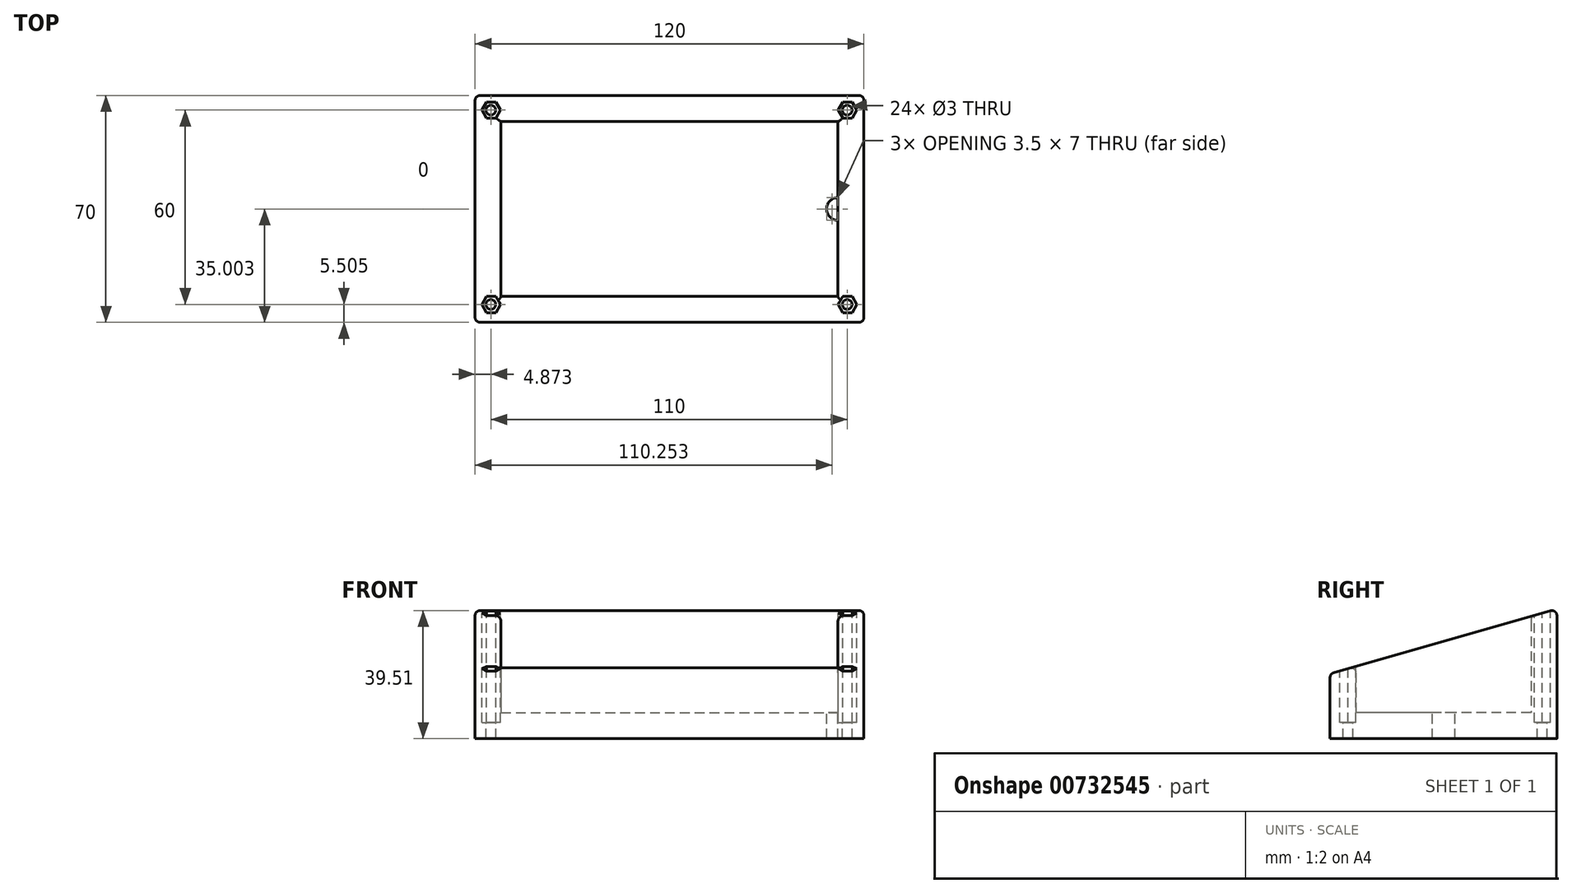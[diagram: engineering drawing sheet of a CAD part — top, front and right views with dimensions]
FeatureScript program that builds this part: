
annotation { "Feature Type Name" : "Feature", "Feature Type Description" : "" }
export const myFeature = defineFeature(function(context is Context, id is Id, definition is map)
    precondition{}
    {
        {
            var Q0;
            Q0=qCreatedBy(makeId("Top.planeOp"),FACE);
            var sketch = newSketch(context, id + "F0", { "sketchPlane" : qUnion([Q0])});
            skLineSegment(sketch, "E0.bottom", {"start": v(-49.4, 44.01) * mm, "end": v(70.6, 44.01) * mm});
            skLineSegment(sketch, "E0.top", {"start": v(-49.4, -25.99) * mm, "end": v(70.6, -25.99) * mm});
            skLineSegment(sketch, "E0.left", {"start": v(-49.4, 44.01) * mm, "end": v(-49.4, -25.99) * mm});
            skLineSegment(sketch, "E0.right", {"start": v(70.6, 44.01) * mm, "end": v(70.6, -25.99) * mm});
            skSolve(sketch);
        }
        {
            var Q0;
            Q0 = qSketchRegion(id + "F0", true);
            extrude(context, id + "F1", {"entities" : qUnion([Q0]), "depth" : 40 * mm, "offsetDistance" : 25 * mm});
        }
        {
            var Q0;
            Q0=makeQuery(id+"F1.opExtrude","SWEPT_FACE",FACE,{"disambiguationData":[OSD([sQuery(id+"F0.wireOp",EDGE,"E0.left")])]});
            var sketch = newSketch(context, id + "F2", { "sketchPlane" : qUnion([Q0])});
            skLineSegment(sketch, "E1", {"start": v(-44.01, 40) * mm, "end": v(25.99, 20) * mm});
            skLineSegment(sketch, "E2", {"start": v(25.99, 20) * mm, "end": v(25.99, 40) * mm});
            skLineSegment(sketch, "E3", {"start": v(25.99, 40) * mm, "end": v(-44.01, 40) * mm});
            skSolve(sketch);
        }
        {
            var Q0;
            Q0 = qSketchRegion(id + "F2", true);
            extrude(context, id + "F3", {"entities" : qUnion([Q0]), "operationType" : NewBodyOperationType.REMOVE, "endBound" : BoundingType.THROUGH_ALL, "oppositeDirection" : true, "depth" : 25 * mm, "offsetDistance" : 25 * mm});
        }
        {
            var Q0;
            Q0=makeQuery(id+"F3.boolean.opBoolean","COPY",FACE,{"derivedFrom":makeQuery(id+"F3.opExtrude","SWEPT_FACE",FACE,{"disambiguationData":[OSD([sQuery(id+"F2.wireOp",EDGE,"E1")])]})});
            shell(context, id + "F4", {"entities" : qUnion([Q0]), "thickness" : 8 * mm});
        }
        {
            var Q0;
            Q0=makeQuery(id+"F1.opExtrude","SWEPT_EDGE",EDGE,{"disambiguationData":[OSD([sQuery(id+"F0.wireOp",EDGE,"E0.top"),sQuery(id+"F0.wireOp",EDGE,"E0.left")])]});
            var Q1;
            Q1=makeQuery(id+"F1.opExtrude","SWEPT_EDGE",EDGE,{"disambiguationData":[OSD([sQuery(id+"F0.wireOp",EDGE,"E0.bottom"),sQuery(id+"F0.wireOp",EDGE,"E0.left")])]});
            var Q2;
            Q2=makeQuery(id+"F1.opExtrude","SWEPT_EDGE",EDGE,{"disambiguationData":[OSD([sQuery(id+"F0.wireOp",EDGE,"E0.bottom"),sQuery(id+"F0.wireOp",EDGE,"E0.right")])]});
            var Q3;
            Q3=makeQuery(id+"F1.opExtrude","SWEPT_EDGE",EDGE,{"disambiguationData":[OSD([sQuery(id+"F0.wireOp",EDGE,"E0.top"),sQuery(id+"F0.wireOp",EDGE,"E0.right")])]});
            var Q4;
            Q4=makeQuery(id+"F3.boolean.opBoolean","COPY",FACE,{"derivedFrom":makeQuery(id+"F3.opExtrude","SWEPT_FACE",FACE,{"disambiguationData":[OSD([sQuery(id+"F2.wireOp",EDGE,"E1")])]})});
            fillet(context, id + "F5", {"entities" : qUnion([Q0, Q1, Q2, Q3, Q4]), "radius" : 1.5 * mm, "tangentPropagation" : true, "allowEdgeOverflow" : false});
        }
        {
            var Q0;
            Q0=qCreatedBy(makeId("Top.planeOp"),FACE);
            cPlane(context, id + "F6", {"entities" : qUnion([Q0]), "cplaneType" : CPlaneType.OFFSET, "offset" : 40 * mm, "width" : 150 * mm, "height" : 150 * mm});
        }
        {
            var Q0;
            Q0=qCreatedBy(id+"F6.planeOp",FACE);
            var sketch = newSketch(context, id + "F7", { "sketchPlane" : qUnion([Q0])});
            skCircle(sketch, "E4.cCircle", {"center": v(-44.47, 39.51) * mm, "radius": 2.5 * mm, "construction": true});
            skLineSegment(sketch, "E4.0", {"start": v(-41.58, 39.51) * mm, "end": v(-43.03, 37.01) * mm});
            skLineSegment(sketch, "E4.1", {"start": v(-43.03, 37.01) * mm, "end": v(-45.91, 37.01) * mm});
            skLineSegment(sketch, "E4.2", {"start": v(-45.91, 37.01) * mm, "end": v(-47.36, 39.51) * mm});
            skLineSegment(sketch, "E4.3", {"start": v(-47.36, 39.51) * mm, "end": v(-45.91, 42.01) * mm});
            skLineSegment(sketch, "E4.4", {"start": v(-45.91, 42.01) * mm, "end": v(-43.03, 42.01) * mm});
            skLineSegment(sketch, "E4.5", {"start": v(-43.03, 42.01) * mm, "end": v(-41.58, 39.51) * mm});
            skPoint(sketch, "E4.0.midPoint", {"position": v(-42.3, 38.26) * mm});
            skCircle(sketch, "E5.cCircle", {"center": v(65.53, 39.51) * mm, "radius": 2.5 * mm, "construction": true});
            skLineSegment(sketch, "E5.0", {"start": v(68.42, 39.51) * mm, "end": v(66.97, 37.01) * mm});
            skLineSegment(sketch, "E5.1", {"start": v(66.97, 37.01) * mm, "end": v(64.09, 37.01) * mm});
            skLineSegment(sketch, "E5.2", {"start": v(64.09, 37.01) * mm, "end": v(62.64, 39.51) * mm});
            skLineSegment(sketch, "E5.3", {"start": v(62.64, 39.51) * mm, "end": v(64.09, 42.01) * mm});
            skLineSegment(sketch, "E5.4", {"start": v(64.09, 42.01) * mm, "end": v(66.97, 42.01) * mm});
            skLineSegment(sketch, "E5.5", {"start": v(66.97, 42.01) * mm, "end": v(68.42, 39.51) * mm});
            skPoint(sketch, "E5.0.midPoint", {"position": v(67.7, 38.26) * mm});
            skCircle(sketch, "E6.cCircle", {"center": v(-44.47, -20.49) * mm, "radius": 2.5 * mm, "construction": true});
            skLineSegment(sketch, "E6.0", {"start": v(-41.58, -20.49) * mm, "end": v(-43.03, -22.99) * mm});
            skLineSegment(sketch, "E6.1", {"start": v(-43.03, -22.99) * mm, "end": v(-45.91, -22.99) * mm});
            skLineSegment(sketch, "E6.2", {"start": v(-45.91, -22.99) * mm, "end": v(-47.36, -20.49) * mm});
            skLineSegment(sketch, "E6.3", {"start": v(-47.36, -20.49) * mm, "end": v(-45.91, -17.99) * mm});
            skLineSegment(sketch, "E6.4", {"start": v(-45.91, -17.99) * mm, "end": v(-43.03, -17.99) * mm});
            skLineSegment(sketch, "E6.5", {"start": v(-43.03, -17.99) * mm, "end": v(-41.58, -20.49) * mm});
            skPoint(sketch, "E6.0.midPoint", {"position": v(-42.3, -21.74) * mm});
            skCircle(sketch, "E7.cCircle", {"center": v(65.53, -20.49) * mm, "radius": 2.5 * mm, "construction": true});
            skLineSegment(sketch, "E7.0", {"start": v(68.42, -20.49) * mm, "end": v(66.97, -22.99) * mm});
            skLineSegment(sketch, "E7.1", {"start": v(66.97, -22.99) * mm, "end": v(64.09, -22.99) * mm});
            skLineSegment(sketch, "E7.2", {"start": v(64.09, -22.99) * mm, "end": v(62.64, -20.49) * mm});
            skLineSegment(sketch, "E7.3", {"start": v(62.64, -20.49) * mm, "end": v(64.09, -17.99) * mm});
            skLineSegment(sketch, "E7.4", {"start": v(64.09, -17.99) * mm, "end": v(66.97, -17.99) * mm});
            skLineSegment(sketch, "E7.5", {"start": v(66.97, -17.99) * mm, "end": v(68.42, -20.49) * mm});
            skPoint(sketch, "E7.0.midPoint", {"position": v(67.7, -21.74) * mm});
            skLineSegment(sketch, "E8.bottom", {"start": v(-44.47, 39.51) * mm, "end": v(65.53, 39.51) * mm, "construction": true});
            skLineSegment(sketch, "E8.top", {"start": v(-44.47, -20.49) * mm, "end": v(65.53, -20.49) * mm, "construction": true});
            skLineSegment(sketch, "E8.left", {"start": v(-44.47, 39.51) * mm, "end": v(-44.47, -20.49) * mm, "construction": true});
            skLineSegment(sketch, "E8.right", {"start": v(65.53, 39.51) * mm, "end": v(65.53, -20.49) * mm, "construction": true});
            skSolve(sketch);
        }
        {
            var Q0;
            Q0 = qSketchRegion(id + "F7", true);
            extrude(context, id + "F8", {"entities" : qUnion([Q0]), "operationType" : NewBodyOperationType.REMOVE, "oppositeDirection" : true, "depth" : 35 * mm, "offsetDistance" : 25 * mm});
        }
        {
            var Q0;
            Q0=qCreatedBy(id+"F6.planeOp",FACE);
            var sketch = newSketch(context, id + "F9", { "sketchPlane" : qUnion([Q0])});
            skLineSegment(sketch, "E9", {"start": v(-47.35, 39.51) * mm, "end": v(-42.1, 39.51) * mm, "construction": true});
            skLineSegment(sketch, "E10", {"start": v(-45.92, 42.01) * mm, "end": v(-43.18, 37.05) * mm, "construction": true});
            skLineSegment(sketch, "E11.bottom", {"start": v(-44.54, 39.51) * mm, "end": v(65.46, 39.51) * mm, "construction": true});
            skLineSegment(sketch, "E11.top", {"start": v(-44.54, -20.49) * mm, "end": v(65.46, -20.49) * mm, "construction": true});
            skLineSegment(sketch, "E11.left", {"start": v(-44.54, 39.51) * mm, "end": v(-44.54, -20.49) * mm, "construction": true});
            skLineSegment(sketch, "E11.right", {"start": v(65.46, 39.51) * mm, "end": v(65.46, -20.49) * mm, "construction": true});
            skLineSegment(sketch, "E12", {"start": v(68.41, -20.49) * mm, "end": v(62.64, -20.49) * mm, "construction": true});
            skLineSegment(sketch, "E13", {"start": v(63.96, -22.98) * mm, "end": v(66.97, -18) * mm, "construction": true});
            skCircle(sketch, "E14", {"center": v(-44.54, 39.51) * mm, "radius": 1.5 * mm});
            skCircle(sketch, "E15", {"center": v(65.46, 39.51) * mm, "radius": 1.5 * mm});
            skCircle(sketch, "E16", {"center": v(65.46, -20.49) * mm, "radius": 1.5 * mm});
            skCircle(sketch, "E17", {"center": v(-44.54, -20.49) * mm, "radius": 1.5 * mm});
            skSolve(sketch);
        }
        {
            var Q0;
            Q0 = qSketchRegion(id + "F9", true);
            extrude(context, id + "F10", {"entities" : qUnion([Q0]), "operationType" : NewBodyOperationType.REMOVE, "endBound" : BoundingType.THROUGH_ALL, "oppositeDirection" : true, "depth" : 25 * mm, "offsetDistance" : 25 * mm});
        }
        {
            var Q0;
            Q0=makeQuery(id+"F4.opShell","OFFSET_FACE",FACE,{"disambiguationData":[OSD([sQuery(id+"F0.wireOp",EDGE,"E0.bottom"),sQuery(id+"F0.wireOp",EDGE,"E0.top"),sQuery(id+"F0.wireOp",EDGE,"E0.left"),sQuery(id+"F0.wireOp",EDGE,"E0.right")])]});
            var sketch = newSketch(context, id + "F11", { "sketchPlane" : qUnion([Q0])});
            skArc(sketch, "E18", {"start": v(62.6, 12.51) * mm, "mid": v(59.1, 9.01) * mm, "end": v(62.6, 5.51) * mm});
            skLineSegment(sketch, "E19", {"start": v(62.6, 12.51) * mm, "end": v(62.6, 5.51) * mm});
            skSolve(sketch);
        }
        {
            var Q0;
            Q0 = qSketchRegion(id + "F11", true);
            extrude(context, id + "F12", {"entities" : qUnion([Q0]), "operationType" : NewBodyOperationType.REMOVE, "oppositeDirection" : true, "depth" : 25 * mm, "offsetDistance" : 25 * mm});
        }
    });
